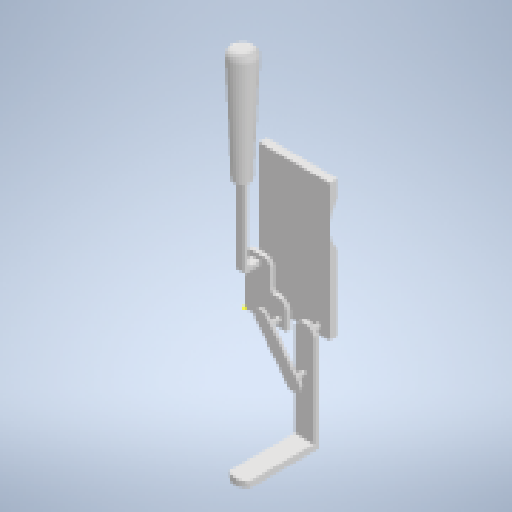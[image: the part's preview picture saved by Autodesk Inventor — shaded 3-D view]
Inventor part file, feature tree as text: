
AUTODESK INVENTOR PART (.ipt)
format: ipt  version: 2023 (Build 270158000, 158)  size: 403,968 bytes
history: native  units: in
note: dims shown in document units (in); Inventor stores cm internally (conversion verified against a paired STEP export)
features: sketch x15, extrude x14, fillet x3, draft x1
ambient origin geometry x8: Origin, YZ Plane, XZ Plane, XY Plane, X Axis, Y Axis, Z Axis, Center Point
bodies: Solid1 (feature_tree)
feature tree (33):
  extrude  "Extrusion1"  Depth=1.6624in
  extrude  "Extrusion2"  TaperAngle=0.0deg  [1 undecoded]
  extrude  "Extrusion3"  Depth=0.1181in TaperAngle=0.0deg
  extrude  "Extrusion4"  Depth=0.315in
  sketch  "Sketch5"  dims[d10=0.315in d11=0.315in]
  extrude  "Extrusion5"  Depth=0.5118in
  extrude  "Extrusion6"  Depth=0.0787in
  extrude  "Extrusion7"  Depth=0.1181in
  extrude  "Extrusion8"  Depth=0.0591in
  sketch  "Sketch10"  dims[d21=0.1181in d22=0.0in d23=0.1181in d24=0.1181in d25=1.1811in]
  extrude  "Extrusion9"  Depth=0.1181in
  fillet  "Fillet1"  Radius=0.1181in
  fillet  "Fillet2"  Radius=1.1811in
  extrude  "Extrusion10"  Depth=0.0591in
  draft  "FaceDraft1"
  fillet  "Fillet3"  Radius=0.1181in
  extrude  "Extrusion11"  Depth=0.0591in
  extrude  "Extrusion12"  Depth=0.0886in
  extrude  "Extrusion13"  Depth=0.0591in
  extrude  "Extrusion14"  Depth=0.0394in
  sketch  "Sketch1"  dims[d0=0.8661in d1=1.6624in]
  sketch  "Sketch3"  dims[d2=0.0984in d3=0.0in d5=0.0in d6=0.0in]
  sketch  "Sketch4"  dims[d7=0.0591in d8=0.1181in d9=0.0in]
  sketch  "Sketch6"  dims[d12=0.6496in d13=0.5118in]
  sketch  "Sketch7"  dims[d14=0.0787in d15=0.0787in]
  sketch  "Sketch8"  dims[d16=0.0394in d17=0.1181in]
  sketch  "Sketch9"  dims[d18=0.0512in d19=0.0in d20=0.0591in]
  sketch  "Sketch11"  dims[d26=0.0591in d27=0.0in d28=0.0591in d29=0.1181in d30=0.0in]
  sketch  "Sketch12"  dims[d31=0.0984in d32=0.0591in]
  sketch  "Sketch13"  dims[d33=0.0591in d34=0.0886in]
  sketch  "Sketch14"  dims[d35=0.1969in d36=0.0in d37=0.0591in]
  sketch  "Sketch15"  dims[d38=0.9252in d39=0.0in d40=0.0394in]
  sketch  "Sketch16"  dims[d41=0.0394in d42=0.0295in d43=0.315in d44=1.378in d45=0.0in d46=0.0172in d47=0.0787in d48=0.5118in d49=0.0591in d50=0.1181in d51=0.0in d52=0.1575in d54=0.0394in d55=0.0in d56=0.0787in d57=0.7874in d58=0.0in d59=0.1737in d60=0.0787in d61=0.0in d62=0.876in d63=0.0in]
note: 1 required parameter value undecoded (feature->parameter linkage not recoverable at this tier; creation-order binding heuristic only, values carry confidence <= 0.55)
